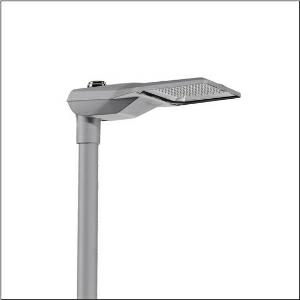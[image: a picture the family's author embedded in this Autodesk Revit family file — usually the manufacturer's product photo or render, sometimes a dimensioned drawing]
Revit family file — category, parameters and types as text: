
# Revit family: streetlight_sl_21_midi___st0_5a_5xe7b37n08mb_20a0
name_source: partatom
category: Lighting Fixtures
units: mm (PartAtom-declared; Revit-internal decimal feet)

## family parameters
Cut with Voids When Loaded = No
Host = Face
Light Source = No
Part Type = Normal
Room Calculation Point = No
Round Connector Dimension = Use Diameter
Shared = No

## types (1)
- --- (1 x LED, 18270 lm, 136 W, 3000K)
    Apparent Load = 136 VA
    CIE Flux Codes = 41 75 97 100 100
    Color Rendering = 70
    Color Temperature = 3000K
    Default Elevation = 1800 mm
    Description = Streetlight SL 21 midi, mast luminaire, primary light control with lens, of PMMA, primary optical cover: cover, of toughened safety glass, transparent, light distribution: ST0.5a, light emission: direct distribution, primary light characteristic: asymmetric, installation type: side-entry, LED, 3G 2.5mm², High Power LED, rated luminous flux: 18.270lm, luminous efficacy: 134lm/W, light colour: 730, colour temperature: 3000K, control gear: NEMA (7pin), control: overheat protection, pre-setting: linear dimming characteristic, constant luminous flux control, time-dependent luminous flux control, flexible luminous flux parameterisation, mains connection: 220..240V, AC, 50/60Hz, connection cable pre-assembled, cable length: 12,5m, wiring characteristics: H05VV-F, start of lifetime: 136W, end of service life: 142W, reduction: 61W, luminaire housing, of diecast aluminium (EN AC-44300), powder-coated, SITECO metallic grey (DB 702S), corrosivity category C5 high according to DIN EN ISO 12944, multi-level sealing system, sealing non-destructively replaceable, inclination adjustable: 0°, 5°, 10°, 15°, length: 644mm, width: 335mm, height: 110mm, spigot size: 42mm (side-entry), mounting height: 4..8m, protection rating (complete): IP66, insulation class (complete): insulation class I (protective earthing), certification: CE, ENEC, ENEC+, VDE, impact resistance: IK10, permissible operating ambient temperature for outdoor applications: -40..+50°C, standard-compliant lighting for roads and squares, packaging unit: 1 piece

Light Distribution: ST0.5a
    Height = 111 mm
    Lamp = 1 x LED
    Lamp Light Flux = 18270 lm
    Lamp Power = 136 W
    Lamp count = 1
    Length = 644 mm
    Luminous efficacy = 134 lm/W
    Manufacturer = Siteco
    ModVariant = No
    Model = 5XE7B37N08MB
    Number of Poles = 1
    OnlyDefault = Yes
    Power Factor = 1
    Product Name = Streetlight SL 21 midi | ST0.5a
    Product group = mast luminaire | pylon top
    ProductGroupID = 6100
    Protection Class = Protection class I
    Protection Degree = IP 66
    RLX_Detail_Level = 1
    RLX_Emergency_Light_Flux = 0 lm
    RLX_Emergency_Type = 0
    RLX_Emergency_Type_DB = No
    RlxData = <blob elided: 37601 chars, md5=89f65561>
    Socket = socket
    Standby Power = 0 W
    System Light Flux = 18270 lm
    System Power = 136 W
    Type Comments = factory setting: luminous flux: 100 % | dim-lin: 254 | 695 mA
    Type Image = l_1294377.jpg
    URL = http://relux.com
    VarID = @adj_136835
    Voltage = 0 V
    Weight = 0.00 kg
    Width = 336 mm

## geometry (parser evidence)
native form markers: Blend x4, Sweep x11
no freeform markers — native parametric forms only
